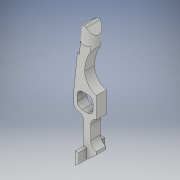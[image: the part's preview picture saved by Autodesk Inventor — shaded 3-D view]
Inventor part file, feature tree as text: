
AUTODESK INVENTOR PART (.ipt)
format: ipt  version: 2018.3 (Build 223284000, 284)  size: 264,192 bytes
history: native  units: in
note: dims shown in document units (in); Inventor stores cm internally (conversion verified against a paired STEP export)
features: extrude x7, sketch x3, revolve x1, plane x1, chamfer x1
ambient origin geometry x8: Origin, YZ Plane, XZ Plane, XY Plane, X Axis, Y Axis, Z Axis, Center Point
bodies: Solid1 (feature_tree)
feature tree (13):
  sketch  "Sketch1"  dims[d0=0.174in d1=0.174in]
  extrude  "Extrusion1"  Depth=0.174in
  revolve  "Revolution1"  [1 undecoded]
  extrude  "Extrusion2"  Depth=0.107in
  extrude  "Extrusion3"  Depth=0.107in
  extrude  "Extrusion4"  Depth=0.107in
  plane  "Work Plane1"
  extrude  "Extrusion5"  Depth=0.107in
  extrude  "Extrusion6"  Depth=0.107in
  extrude  "Extrusion7"  Depth=0.107in
  chamfer  "Chamfer1"  Distance=0.3298in
  sketch  "Sketch3"  dims[d2=0.055in d3=0.19in]
  sketch  "Sketch4"  dims[d4=0.038in d5=1.1956in d6=0.004in d7=0.06in d8=0.08in d9=0.08in d10=0.03in d11=0.3298in d12=0.476in d13=0.34in d14=0.205in d15=0.079in d16=0.78in d17=0.337in d19=0.035in d20=0.06in d21=0.05in d22=0.109in d23=0.2886in d24=0.3023in d25=0.03in d26=0.015in d27=0.739in d28=0.21in d29=0.038in d30=0.155in d32=0.051in d33=0.0775in d34=0.312in d35=0.0775in d36=90.0deg d37=0.107in d38=0.0in d39=0.47in d40=0.0535in d41=0.2945in d42=0.0in d43=0.107in d44=0.0in d45=0.107in d46=0.0in d47=0.0in d48=0.312in d49=0.0in d50=0.312in d51=0.0in d52=0.285in d53=0.0in d54=0.012in d55=0.125in d56=45.0deg]
note: 1 required parameter value undecoded (feature->parameter linkage not recoverable at this tier; creation-order binding heuristic only, values carry confidence <= 0.55)
